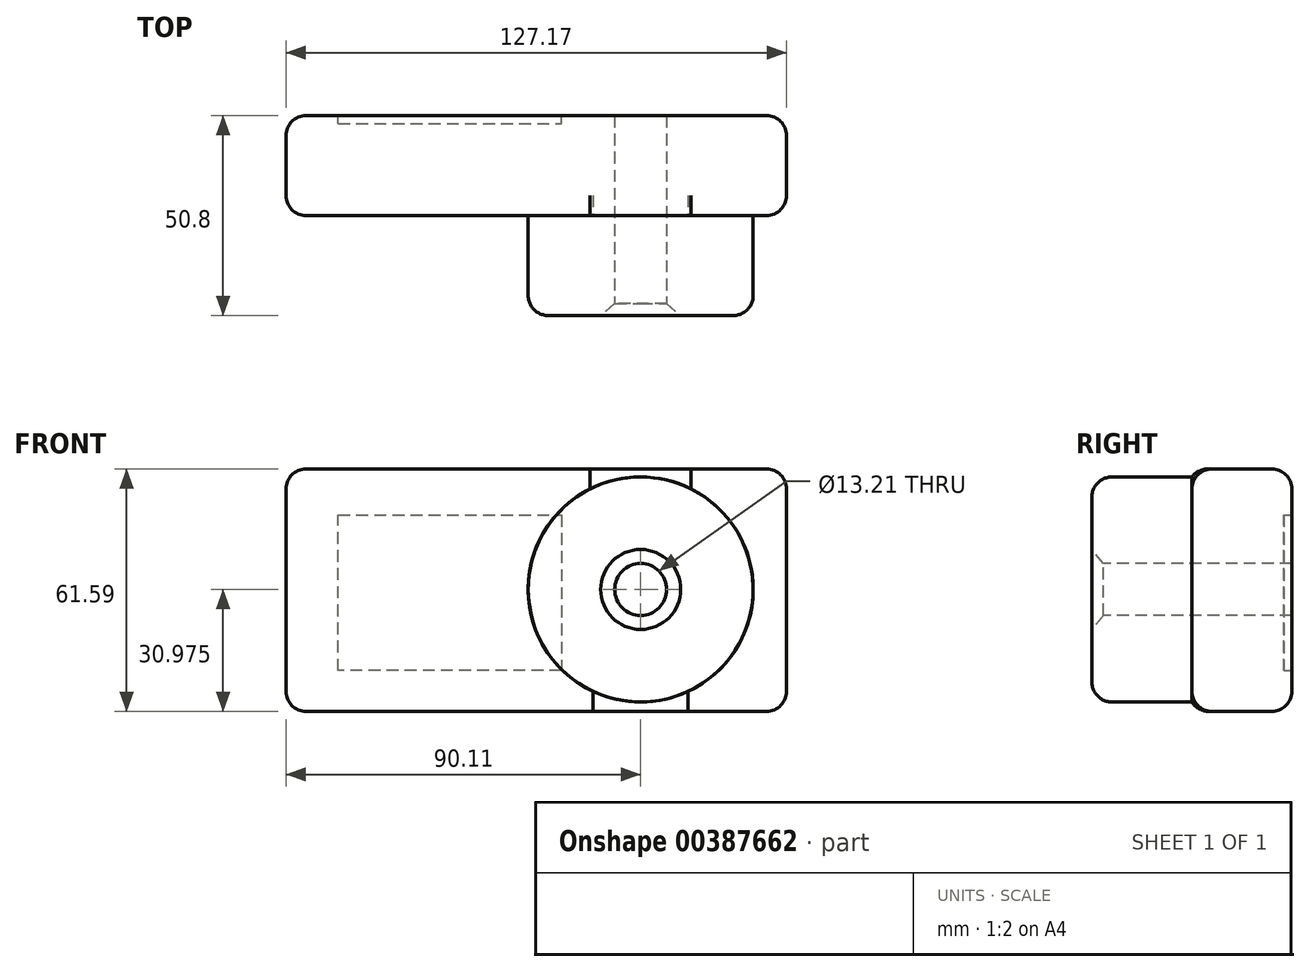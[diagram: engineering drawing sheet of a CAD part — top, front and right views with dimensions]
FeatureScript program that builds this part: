
annotation { "Feature Type Name" : "Feature", "Feature Type Description" : "" }
export const myFeature = defineFeature(function(context is Context, id is Id, definition is map)
    precondition{}
    {
        {
            var Q0;
            Q0=qCreatedBy(makeId("Front.planeOp"),FACE);
            var sketch = newSketch(context, id + "F0", { "sketchPlane" : qUnion([Q0])});
            skLineSegment(sketch, "E0.bottom", {"start": v(-57.57, 34.98) * mm, "end": v(69.6, 34.98) * mm});
            skLineSegment(sketch, "E0.top", {"start": v(-57.57, -26.61) * mm, "end": v(69.6, -26.61) * mm});
            skLineSegment(sketch, "E0.left", {"start": v(-57.57, 34.98) * mm, "end": v(-57.57, -26.61) * mm});
            skLineSegment(sketch, "E0.right", {"start": v(69.6, 34.98) * mm, "end": v(69.6, -26.61) * mm});
            skSolve(sketch);
        }
        {
            var Q0;
            Q0=makeQuery(id+"F0.imprint","IMPRINT",FACE,{"disambiguationData":[TD([[makeQuery(id+"F0.imprint","IMPRINT",EDGE,{"derivedFrom":sQuery(id+"F0.wireOp",EDGE,"E0.bottom")}),-1.0]])]});
            extrude(context, id + "F1", {"entities" : qUnion([Q0]), "depth" : 25.4 * mm});
        }
        {
            var Q0;
            Q0=makeQuery(id+"F1.opExtrude","CAP_FACE",FACE,{"disambiguationData":[OSD([sQuery(id+"F0.wireOp",EDGE,"E0.bottom"),sQuery(id+"F0.wireOp",EDGE,"E0.top"),sQuery(id+"F0.wireOp",EDGE,"E0.left"),sQuery(id+"F0.wireOp",EDGE,"E0.right")])],"isStart":false});
            var sketch = newSketch(context, id + "F2", { "sketchPlane" : qUnion([Q0])});
            skCircle(sketch, "E1", {"center": v(32.54, 4.37) * mm, "radius": 28.58 * mm});
            skSolve(sketch);
        }
        {
            var Q0;
            Q0=makeQuery(id+"F2.imprint","IMPRINT",FACE,{"disambiguationData":[TD([[makeQuery(id+"F2.imprint","IMPRINT",EDGE,{"derivedFrom":sQuery(id+"F2.wireOp",EDGE,"E1")}),1.0]])]});
            extrude(context, id + "F3", {"entities" : qUnion([Q0]), "operationType" : NewBodyOperationType.ADD, "depth" : 25.4 * mm});
        }
        {
            var Q0;
            Q0=makeQuery(id+"F3.opExtrude","CAP_EDGE",EDGE,{"disambiguationData":[OSD([sQuery(id+"F2.wireOp",EDGE,"E1")])],"isStart":false});
            fillet(context, id + "F4", {"entities" : qUnion([Q0]), "radius" : 5.08 * mm, "tangentPropagation" : true, "allowEdgeOverflow" : false});
        }
        {
            var Q0;
            Q0=makeQuery(id+"F3.opExtrude","CAP_FACE",FACE,{"disambiguationData":[OSD([sQuery(id+"F2.wireOp",EDGE,"E1")])],"isStart":false});
            var sketch = newSketch(context, id + "F5", { "sketchPlane" : qUnion([Q0])});
            skCircle(sketch, "E2", {"center": v(32.54, 4.37) * mm, "radius": 6.5 * mm});
            skSolve(sketch);
        }
        {
            var Q0;
            Q0=sQuery(id+"F5.wireOp",VERTEX,"E2.center");
            var Q1;
            Q1=makeQuery(id+"F1.opExtrude","SWEPT_BODY",BODY,{"disambiguationData":[OSD([sQuery(id+"F0.wireOp",EDGE,"E0.bottom"),sQuery(id+"F0.wireOp",EDGE,"E0.top"),sQuery(id+"F0.wireOp",EDGE,"E0.left"),sQuery(id+"F0.wireOp",EDGE,"E0.right")])]});
            hole(context, id + "F6", {"style" : HoleStyle.C_SINK, "endStyle" : HoleEndStyle.THROUGH, "holeDiameter" : 13.2 * mm, "cSinkDiameter" : 20.32 * mm, "cSinkAngle" : 100 * degree, "isTappedThrough" : true, "tappedDepth" : 12.7 * mm, "tapClearance" : 3, "startFromSketch" : true, "locations" : qUnion([Q0]), "scope" : qUnion([Q1])});
        }
        {
            var Q0;
            Q0=makeQuery(id+"F1.opExtrude","CAP_EDGE",EDGE,{"disambiguationData":[OSD([sQuery(id+"F0.wireOp",EDGE,"E0.left")])],"isStart":false});
            var Q1;
            Q1=makeQuery(id+"F1.opExtrude","CAP_EDGE",EDGE,{"disambiguationData":[OSD([sQuery(id+"F0.wireOp",EDGE,"E0.bottom")])],"isStart":false});
            var Q2;
            Q2=makeQuery(id+"F1.opExtrude","CAP_EDGE",EDGE,{"disambiguationData":[OSD([sQuery(id+"F0.wireOp",EDGE,"E0.right")])],"isStart":false});
            var Q3;
            Q3=makeQuery(id+"F1.opExtrude","CAP_EDGE",EDGE,{"disambiguationData":[OSD([sQuery(id+"F0.wireOp",EDGE,"E0.top")])],"isStart":false});
            fillet(context, id + "F7", {"entities" : qUnion([Q0, Q1, Q2, Q3]), "radius" : 5.08 * mm, "tangentPropagation" : true, "allowEdgeOverflow" : false});
        }
        {
            var Q0;
            Q0=makeQuery(id+"F1.opExtrude","SWEPT_EDGE",EDGE,{"disambiguationData":[OSD([sQuery(id+"F0.wireOp",EDGE,"E0.bottom"),sQuery(id+"F0.wireOp",EDGE,"E0.right")])]});
            var Q1;
            Q1=makeQuery(id+"F1.opExtrude","CAP_EDGE",EDGE,{"disambiguationData":[OSD([sQuery(id+"F0.wireOp",EDGE,"E0.right")])],"isStart":true});
            var Q2;
            Q2=makeQuery(id+"F1.opExtrude","CAP_EDGE",EDGE,{"disambiguationData":[OSD([sQuery(id+"F0.wireOp",EDGE,"E0.bottom")])],"isStart":true});
            var Q3;
            Q3=makeQuery(id+"F1.opExtrude","CAP_EDGE",EDGE,{"disambiguationData":[OSD([sQuery(id+"F0.wireOp",EDGE,"E0.left")])],"isStart":true});
            var Q4;
            Q4=makeQuery(id+"F1.opExtrude","CAP_EDGE",EDGE,{"disambiguationData":[OSD([sQuery(id+"F0.wireOp",EDGE,"E0.top")])],"isStart":true});
            var Q5;
            Q5=makeQuery(id+"F1.opExtrude","SWEPT_EDGE",EDGE,{"disambiguationData":[OSD([sQuery(id+"F0.wireOp",EDGE,"E0.top"),sQuery(id+"F0.wireOp",EDGE,"E0.right")])]});
            var Q6;
            Q6=makeQuery(id+"F1.opExtrude","SWEPT_EDGE",EDGE,{"disambiguationData":[OSD([sQuery(id+"F0.wireOp",EDGE,"E0.bottom"),sQuery(id+"F0.wireOp",EDGE,"E0.left")])]});
            var Q7;
            Q7=makeQuery(id+"F1.opExtrude","SWEPT_EDGE",EDGE,{"disambiguationData":[OSD([sQuery(id+"F0.wireOp",EDGE,"E0.top"),sQuery(id+"F0.wireOp",EDGE,"E0.left")])]});
            var Q8;
            Q8=makeQuery(id+"F6.hole-0.boolean.opBoolean","INTERSECT",EDGE,{"derivedFrom":[makeQuery(id+"F1.opExtrude","CAP_FACE",FACE,{"disambiguationData":[OSD([sQuery(id+"F0.wireOp",EDGE,"E0.bottom"),sQuery(id+"F0.wireOp",EDGE,"E0.top"),sQuery(id+"F0.wireOp",EDGE,"E0.left"),sQuery(id+"F0.wireOp",EDGE,"E0.right")])],"isStart":true}),makeQuery(id+"F6.hole-0.opRevolve","SWEPT_FACE",FACE,{"disambiguationData":[OSD([sQuery(id+"F6.hole-0.sketch.wireOp",EDGE,"core_line_2")])]})]});
            var Q9;
            Q9=makeQuery(id+"F6.hole-0.boolean.opBoolean","COPY",EDGE,{"derivedFrom":makeQuery(id+"F6.hole-0.opRevolve","SWEPT_EDGE",EDGE,{"disambiguationData":[OSD([sQuery(id+"F6.hole-0.sketch.wireOp",EDGE,"csink_start_line_1"),sQuery(id+"F6.hole-0.sketch.wireOp",EDGE,"core_line_2")])]})});
            fillet(context, id + "F8", {"entities" : qUnion([Q0, Q1, Q2, Q3, Q4, Q5, Q6, Q7, Q8, Q9]), "radius" : 5.08 * mm, "tangentPropagation" : true, "allowEdgeOverflow" : false});
        }
        {
            var Q0;
            Q0=makeQuery(id+"F1.opExtrude","CAP_FACE",FACE,{"disambiguationData":[OSD([sQuery(id+"F0.wireOp",EDGE,"E0.bottom"),sQuery(id+"F0.wireOp",EDGE,"E0.top"),sQuery(id+"F0.wireOp",EDGE,"E0.left"),sQuery(id+"F0.wireOp",EDGE,"E0.right")])],"isStart":true});
            var sketch = newSketch(context, id + "F9", { "sketchPlane" : qUnion([Q0])});
            skLineSegment(sketch, "E3", {"start": v(-12.41, 23.3) * mm, "end": v(-12.41, -16.23) * mm});
            skLineSegment(sketch, "E4", {"start": v(-12.41, -16.23) * mm, "end": v(44.3, -16.23) * mm});
            skLineSegment(sketch, "E5", {"start": v(44.3, -16.23) * mm, "end": v(44.3, 23.3) * mm});
            skLineSegment(sketch, "E6", {"start": v(44.3, 23.3) * mm, "end": v(-12.41, 23.3) * mm});
            skSolve(sketch);
        }
        {
            var Q0;
            Q0 = qSketchRegion(id + "F9", true);
            extrude(context, id + "F10", {"entities" : qUnion([Q0]), "operationType" : NewBodyOperationType.REMOVE, "oppositeDirection" : true, "depth" : 2.03 * mm});
        }
    });
